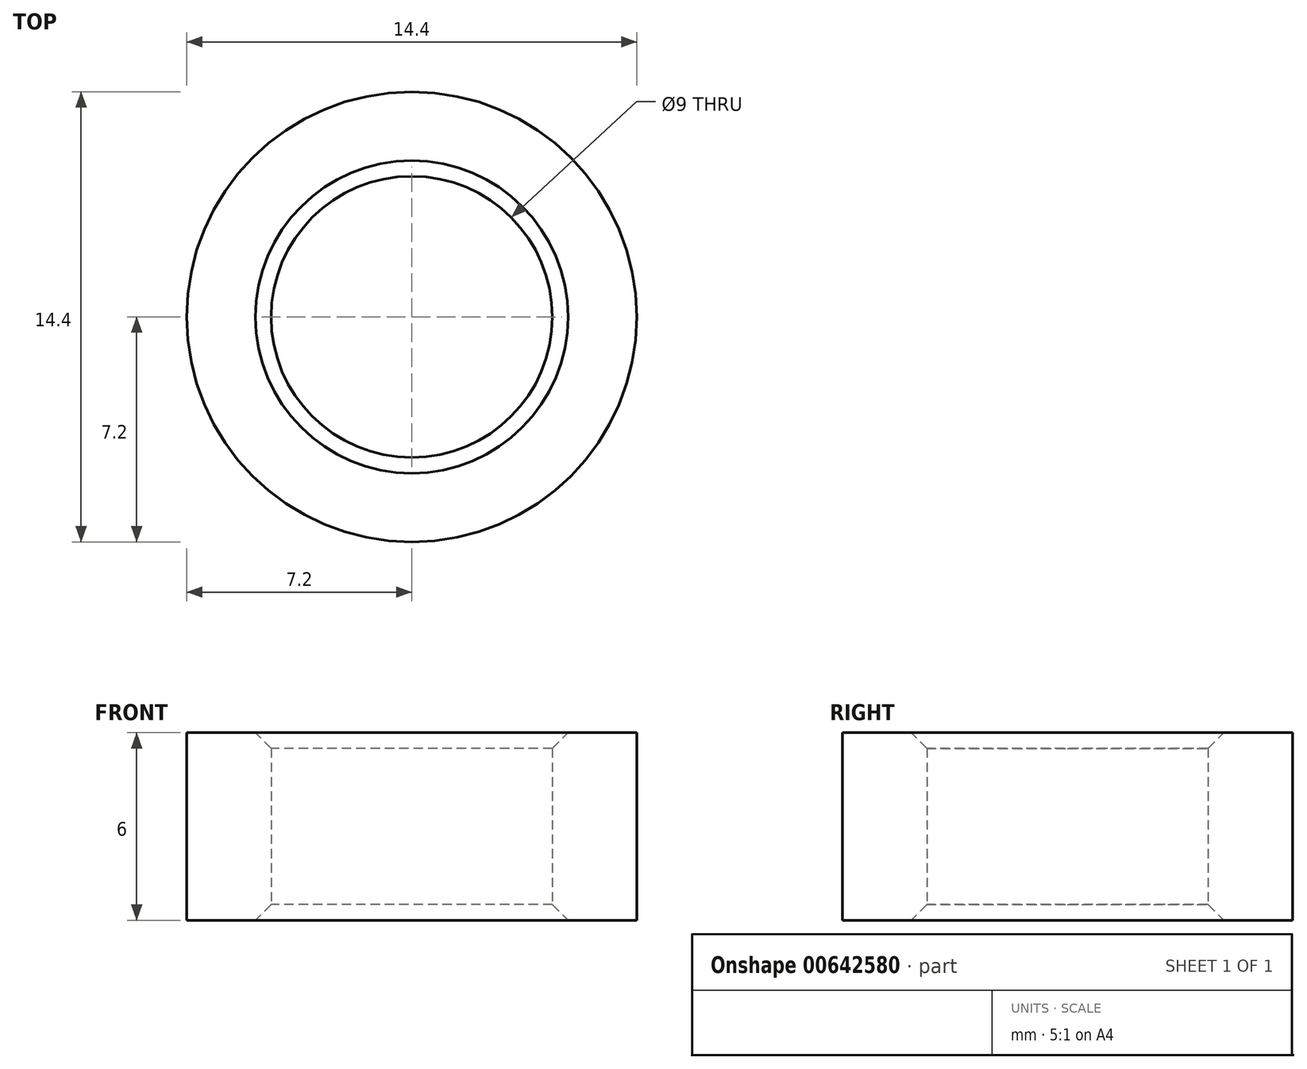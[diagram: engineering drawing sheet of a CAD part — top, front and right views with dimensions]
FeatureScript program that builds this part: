
annotation { "Feature Type Name" : "Feature", "Feature Type Description" : "" }
export const myFeature = defineFeature(function(context is Context, id is Id, definition is map)
    precondition{}
    {
        {
            var Q0;
            Q0=qCreatedBy(makeId("Top.planeOp"),FACE);
            var sketch = newSketch(context, id + "F0", { "sketchPlane" : qUnion([Q0])});
            skCircle(sketch, "E0", {"center": v(0, 0) * mm, "radius": 4.5 * mm});
            skCircle(sketch, "E1", {"center": v(0, 0) * mm, "radius": 7.2 * mm});
            skCircle(sketch, "E2", {"center": v(0, 0) * mm, "radius": 4 * mm});
            skSolve(sketch);
        }
        {
            var Q0;
            Q0=makeQuery(id+"F0.imprint","IMPRINT",FACE,{"disambiguationData":[TD([[makeQuery(id+"F0.imprint","IMPRINT",EDGE,{"derivedFrom":sQuery(id+"F0.wireOp",EDGE,"E0")}),-1.0]])]});
            extrude(context, id + "F1", {"entities" : qUnion([Q0]), "depth" : 6 * mm, "offsetDistance" : 25 * mm});
        }
        {
            var Q0;
            Q0=makeQuery(id+"F1.opExtrude","CAP_EDGE",EDGE,{"disambiguationData":[OSD([sQuery(id+"F0.wireOp",EDGE,"E0")])],"isStart":false});
            var Q1;
            Q1=makeQuery(id+"F1.opExtrude","CAP_EDGE",EDGE,{"disambiguationData":[OSD([sQuery(id+"F0.wireOp",EDGE,"E0")])],"isStart":true});
            chamfer(context, id + "F2", {"entities" : qUnion([Q0, Q1]), "chamferType" : ChamferType.OFFSET_ANGLE, "width" : 0.5 * mm, "oppositeDirection" : false, "angle" : 45 * degree, "tangentPropagation" : true});
        }
    });
